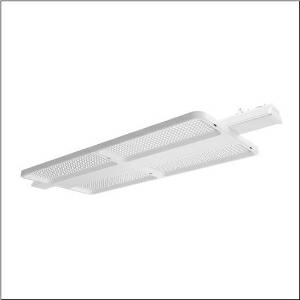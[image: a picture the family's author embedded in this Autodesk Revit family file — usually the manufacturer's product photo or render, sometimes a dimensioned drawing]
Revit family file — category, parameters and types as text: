
# Revit family: highbay_21_fur_licross_r__tragschiene_maxi_52hn11db6qla_fd5b
name_source: partatom
category: Lighting Fixtures
units: mm (PartAtom-declared; Revit-internal decimal feet)

## family parameters
Cut with Voids When Loaded = No
Host = Face
Light Source = No
Part Type = Normal
Room Calculation Point = No
Round Connector Dimension = Use Diameter
Shared = No

## types (1)
- --- (1 x LED, 5650 lm, 31.4 W, 6500K)
    Apparent Load = 31 VA
    CIE Flux Codes = 89 97 99 100 100
    Color Rendering = 80
    Color Temperature = 6500K
    Default Elevation = 1800 mm
    Description = high bay luminaire Highbay 21 for Licross® trunking rail maxi; direct symmetric narrow distribution, light control with lens of PMMA; UGR ≤ 22 (X = 4H | Y = 8H | S = 0.25H | reflection values 70/50/20); luminous flux: 36.840lm; light colour: 865, colour temperature: 6500K, MacAdam ≤ 3 SDCM (initial), colour rendering: CRI > 80; luminous efficacy: 186,3lm/W; rated service life: 75.000h (L80/B50) at AT= ta max; control: DALI 2; luminaire connection: plug, 5-pole, with phase selectionmains connection: 230..240V, AC 50/60Hz; connected load: 197,7W; protection rating (complete): IP64; insulation class (complete): insulation class I (protective earthing); protection symbol: D; impact resistance: IK07; certification: CE, ENEC, VDE, UKCA; internal wiring halogen-free; luminaire corresponds to IFS (International Featured Standards) requirements for safety and quality in the food industry; LABS conformity tested according to VDMA 24364:2018-05; housing frame of high-performance plastic PA6, matt traffic white (RAL 9016); cover of PMMA; fixing on rail side of steel, galvanised, white; blank cover of PC/ABS, traffic white (RAL 9016); dimension (LxWxH): 1.250 x 442 x 71mm; permissible operating ambient temperature: -40..+55°C (reducing of maximum allowable ambient temperature of 5°C with ceiling mounting); packaging unit: 1 piece
    Height = 72 mm  [stored 0.23622 ft]
    Lamp = 1 x LED
    Lamp Light Flux = 5650 lm
    Lamp Power = 31.4 W
    Lamp count = 1
    Length = 946 mm
    Luminous efficacy = 180 lm/W
    Manufacturer = Siteco
    ModVariant = No
    Model = 52HN11DB6QLA
    Mounting Place = Ceiling
    Mounting Type = Pendant
    Number of Poles = 1
    OnlyDefault = Yes
    Power Factor = 1
    Product Name = Highbay 21 für Licross® Tragschiene maxi
    Product group = high bay luminaire
    ProductGroupID = 901
    Protection Class = Protection class I
    Protection Degree = IP 64
    RLX_Detail_Level = 1
    RLX_Emergency_Light_Flux = 0 lm
    RLX_Emergency_Type = 0
    RLX_Emergency_Type_DB = No
    RlxData = <blob elided: 130121 chars, md5=a62b00ad>
    Socket = socket
    Standby Power = 0 W
    System Light Flux = 5650 lm
    System Power = 31 W
    Type Comments = : DC mode (central or group accumulator) initial emergency light level
    Type Image = l_1361711.jpg
    URL = http://relux.com
    VarID = @adj_000985
    Voltage = 0 V
    Weight = 0.00 kg
    Width = 442 mm

note: [stored X ft] marks values corroborated as IEEE doubles in the binary element streams (Revit-internal decimal feet)

## geometry (parser evidence)
native form markers: Blend x4, Sweep x10
no freeform markers — native parametric forms only
